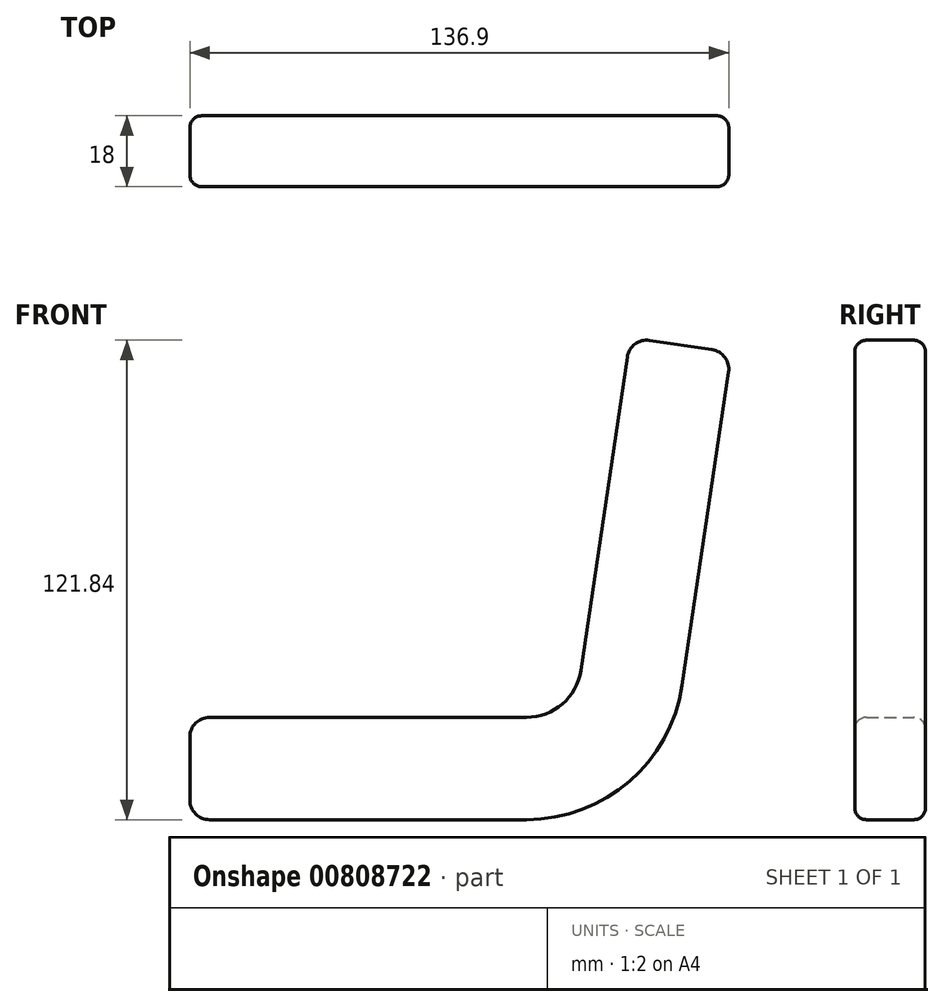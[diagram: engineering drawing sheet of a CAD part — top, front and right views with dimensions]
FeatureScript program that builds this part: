
annotation { "Feature Type Name" : "Feature", "Feature Type Description" : "" }
export const myFeature = defineFeature(function(context is Context, id is Id, definition is map)
    precondition{}
    {
        {
            var Q0;
            Q0=qCreatedBy(makeId("Front.planeOp"),FACE);
            var sketch = newSketch(context, id + "F0", { "sketchPlane" : qUnion([Q0])});
            skLineSegment(sketch, "E0", {"start": v(-115, 0) * mm, "end": v(-34.51, 0) * mm});
            skLineSegment(sketch, "E1", {"start": v(5.06, 34.14) * mm, "end": v(16.84, 113.76) * mm});
            skPoint(sketch, "E2.end.orphan", {"position": v(0, 72.89) * mm});
            skPoint(sketch, "E3.visualSharp", {"position": v(0, 0) * mm});
            skArc(sketch, "E3.filletArc", {"start": v(-34.51, 0) * mm, "mid": v(-8.38, 9.72) * mm, "end": v(5.06, 34.14) * mm});
            skLineSegment(sketch, "E4.0", {"start": v(-20.66, 37.95) * mm, "end": v(-8.88, 117.57) * mm});
            skArc(sketch, "E4.1", {"start": v(-34.51, 26) * mm, "mid": v(-25.37, 29.4) * mm, "end": v(-20.66, 37.95) * mm});
            skLineSegment(sketch, "E4.2", {"start": v(-115, 26) * mm, "end": v(-34.51, 26) * mm});
            skLineSegment(sketch, "E5", {"start": v(-3.2, 121.78) * mm, "end": v(12.63, 119.44) * mm});
            skLineSegment(sketch, "E6", {"start": v(-120, 21) * mm, "end": v(-120, 5) * mm});
            skPoint(sketch, "E7.visualSharp", {"position": v(-8.14, 122.51) * mm});
            skArc(sketch, "E7.filletArc", {"start": v(-3.2, 121.78) * mm, "mid": v(-6.9, 120.85) * mm, "end": v(-8.88, 117.57) * mm});
            skPoint(sketch, "E8.visualSharp", {"position": v(17.58, 118.7) * mm});
            skArc(sketch, "E8.filletArc", {"start": v(16.84, 113.76) * mm, "mid": v(15.91, 117.47) * mm, "end": v(12.63, 119.44) * mm});
            skPoint(sketch, "E9.visualSharp", {"position": v(-120, 26) * mm});
            skArc(sketch, "E9.filletArc", {"start": v(-115, 26) * mm, "mid": v(-118.54, 24.54) * mm, "end": v(-120, 21) * mm});
            skPoint(sketch, "E10.visualSharp", {"position": v(-120, 0) * mm});
            skArc(sketch, "E10.filletArc", {"start": v(-120, 5) * mm, "mid": v(-118.54, 1.46) * mm, "end": v(-115, 0) * mm});
            skSolve(sketch);
        }
        {
            var Q0;
            Q0=makeQuery(id+"F0.imprint","IMPRINT",FACE,{"disambiguationData":[TD([[makeQuery(id+"F0.imprint","IMPRINT",EDGE,{"derivedFrom":sQuery(id+"F0.wireOp",EDGE,"E0")}),1.0]])]});
            extrude(context, id + "F1", {"entities" : qUnion([Q0]), "depth" : 18 * mm, "offsetDistance" : 25 * mm});
        }
        {
            var Q0;
            Q0=makeQuery(id+"F1.opExtrude","CAP_FACE",FACE,{"disambiguationData":[OSD([sQuery(id+"F0.wireOp",EDGE,"E0"),sQuery(id+"F0.wireOp",EDGE,"E1"),sQuery(id+"F0.wireOp",EDGE,"E3.filletArc"),sQuery(id+"F0.wireOp",EDGE,"E4.0"),sQuery(id+"F0.wireOp",EDGE,"E4.1"),sQuery(id+"F0.wireOp",EDGE,"E4.2"),sQuery(id+"F0.wireOp",EDGE,"E5"),sQuery(id+"F0.wireOp",EDGE,"E6"),sQuery(id+"F0.wireOp",EDGE,"E7.filletArc"),sQuery(id+"F0.wireOp",EDGE,"E8.filletArc"),sQuery(id+"F0.wireOp",EDGE,"E9.filletArc"),sQuery(id+"F0.wireOp",EDGE,"E10.filletArc")])],"isStart":false});
            var Q1;
            Q1=makeQuery(id+"F1.opExtrude","CAP_FACE",FACE,{"disambiguationData":[OSD([sQuery(id+"F0.wireOp",EDGE,"E0"),sQuery(id+"F0.wireOp",EDGE,"E1"),sQuery(id+"F0.wireOp",EDGE,"E3.filletArc"),sQuery(id+"F0.wireOp",EDGE,"E4.0"),sQuery(id+"F0.wireOp",EDGE,"E4.1"),sQuery(id+"F0.wireOp",EDGE,"E4.2"),sQuery(id+"F0.wireOp",EDGE,"E5"),sQuery(id+"F0.wireOp",EDGE,"E6"),sQuery(id+"F0.wireOp",EDGE,"E7.filletArc"),sQuery(id+"F0.wireOp",EDGE,"E8.filletArc"),sQuery(id+"F0.wireOp",EDGE,"E9.filletArc"),sQuery(id+"F0.wireOp",EDGE,"E10.filletArc")])],"isStart":true});
            fillet(context, id + "F2", {"entities" : qUnion([Q0, Q1]), "radius" : 3 * mm, "tangentPropagation" : true, "allowEdgeOverflow" : false});
        }
    });
